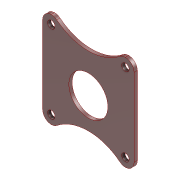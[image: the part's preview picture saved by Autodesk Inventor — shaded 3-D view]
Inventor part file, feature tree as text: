
AUTODESK INVENTOR PART (.ipt)
format: ipt  version: 2020 (Build 240168000, 168)  size: 198,144 bytes
history: native  units: mm
features: extrude x5, sketch x5, mirror x3, other x3, fillet x2, reference x1, projected_geometry x1
ambient origin geometry x8: Origin, YZ Plane, XZ Plane, XY Plane, X Axis, Y Axis, Z Axis, Center Point
bodies: Body1 (feature_tree)
feature tree (20):
  extrude  "Extrusion3"  Depth=42.0mm
  extrude  "Extrusion4"  Depth=1.5mm
  fillet  "Fillet2"  Radius=3.0mm
  mirror  "Mirror2"
  mirror  "Mirror3"
  extrude  "Extrusion5"  TaperAngle=0.0deg  [1 undecoded]
  mirror  "Mirror4"
  fillet  "Fillet3"  Radius=3.0mm
  extrude  "Extrusion6"  Depth=1.5mm TaperAngle=0.0deg
  extrude  "Extrusion7"  TaperAngle=0.0deg  [1 undecoded]
  sketch  "Sketch3"  dims[d24=40.2mm d25=42.0mm]
  sketch  "Sketch4"  dims[d26=1.5mm d27=0.0mm d28=3.0mm d29=3.0mm]
  sketch  "Sketch5"  dims[d30=3.4mm d31=0.0mm d32=0.0mm d33=3.0mm]
  sketch  "Sketch7"  dims[d34=3.0mm d35=1.5mm d36=0.0mm]
  reference  "Reference1"
  sketch  "Sketch8"  dims[d37=3.0mm d39=0.0mm d40=0.0mm d41=18.0mm d42=1.1mm d43=1.1mm d44=1.0mm d45=10.0mm d46=0.0mm]
  projected_geometry  "Projected Loop1"
  other  "<userpath>\Google Drive\Breathney\oxymount.iam"
  other  "oxymount.iam"
  other  "oxysens:1"
note: 2 required parameter values undecoded (feature->parameter linkage not recoverable at this tier; creation-order binding heuristic only, values carry confidence <= 0.55)
